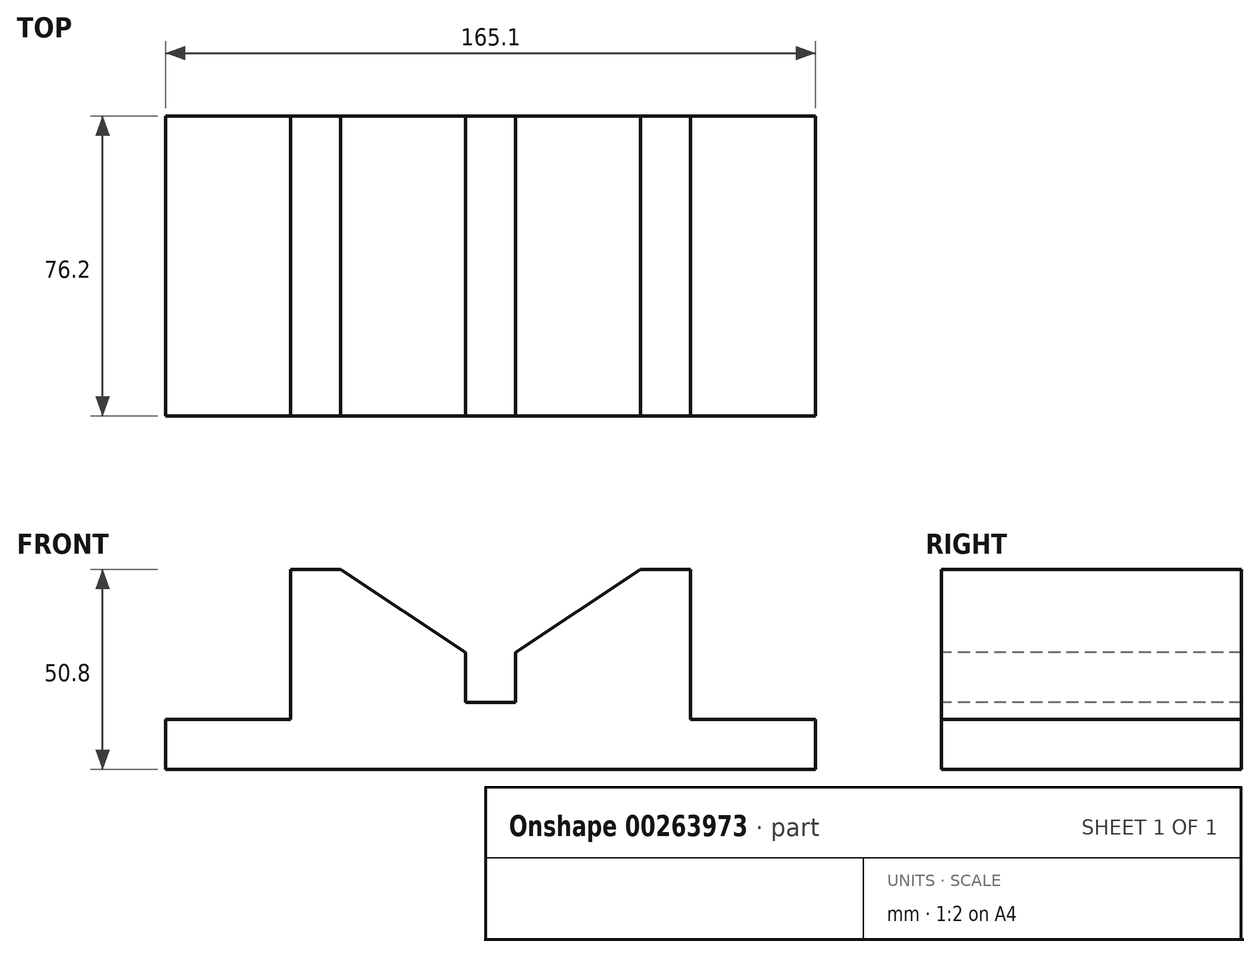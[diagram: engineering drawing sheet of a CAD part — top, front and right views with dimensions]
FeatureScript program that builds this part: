
annotation { "Feature Type Name" : "Feature", "Feature Type Description" : "" }
export const myFeature = defineFeature(function(context is Context, id is Id, definition is map)
    precondition{}
    {
        {
            var Q0;
            Q0=qCreatedBy(makeId("Front.planeOp"),FACE);
            var sketch = newSketch(context, id + "F0", { "sketchPlane" : qUnion([Q0])});
            skLineSegment(sketch, "E0", {"start": v(-76.2, 0) * mm, "end": v(76.2, 0) * mm});
            skLineSegment(sketch, "E1", {"start": v(76.2, 0) * mm, "end": v(76.2, 12.7) * mm});
            skLineSegment(sketch, "E2", {"start": v(76.2, 12.7) * mm, "end": v(44.45, 12.7) * mm});
            skLineSegment(sketch, "E3", {"start": v(44.45, 12.7) * mm, "end": v(44.45, 50.8) * mm});
            skLineSegment(sketch, "E4", {"start": v(44.45, 50.8) * mm, "end": v(31.75, 50.8) * mm});
            skLineSegment(sketch, "E5", {"start": v(31.75, 50.8) * mm, "end": v(0, 29.74) * mm});
            skLineSegment(sketch, "E6", {"start": v(0, 29.74) * mm, "end": v(0, 17.04) * mm});
            skLineSegment(sketch, "E7", {"start": v(0, 17.04) * mm, "end": v(-12.7, 17.04) * mm});
            skLineSegment(sketch, "E8", {"start": v(-12.7, 17.04) * mm, "end": v(-12.7, 29.74) * mm});
            skLineSegment(sketch, "E9", {"start": v(-12.7, 29.74) * mm, "end": v(-44.45, 50.8) * mm});
            skLineSegment(sketch, "E10", {"start": v(-44.45, 50.8) * mm, "end": v(-57.15, 50.8) * mm});
            skLineSegment(sketch, "E11", {"start": v(-57.15, 50.8) * mm, "end": v(-57.15, 12.7) * mm});
            skLineSegment(sketch, "E12", {"start": v(-57.15, 12.7) * mm, "end": v(-88.9, 12.7) * mm});
            skLineSegment(sketch, "E13", {"start": v(-88.9, 12.7) * mm, "end": v(-88.9, 0) * mm});
            skLineSegment(sketch, "E14", {"start": v(-88.9, 0) * mm, "end": v(-76.2, 0) * mm});
            skSolve(sketch);
        }
        {
            var Q0;
            Q0=makeQuery(id+"F0.imprint","IMPRINT",FACE,{"disambiguationData":[TD([[makeQuery(id+"F0.imprint","IMPRINT",EDGE,{"derivedFrom":sQuery(id+"F0.wireOp",EDGE,"E0")}),1.0]])]});
            extrude(context, id + "F1", {"entities" : qUnion([Q0]), "oppositeDirection" : true, "depth" : 76.2 * mm});
        }
    });
